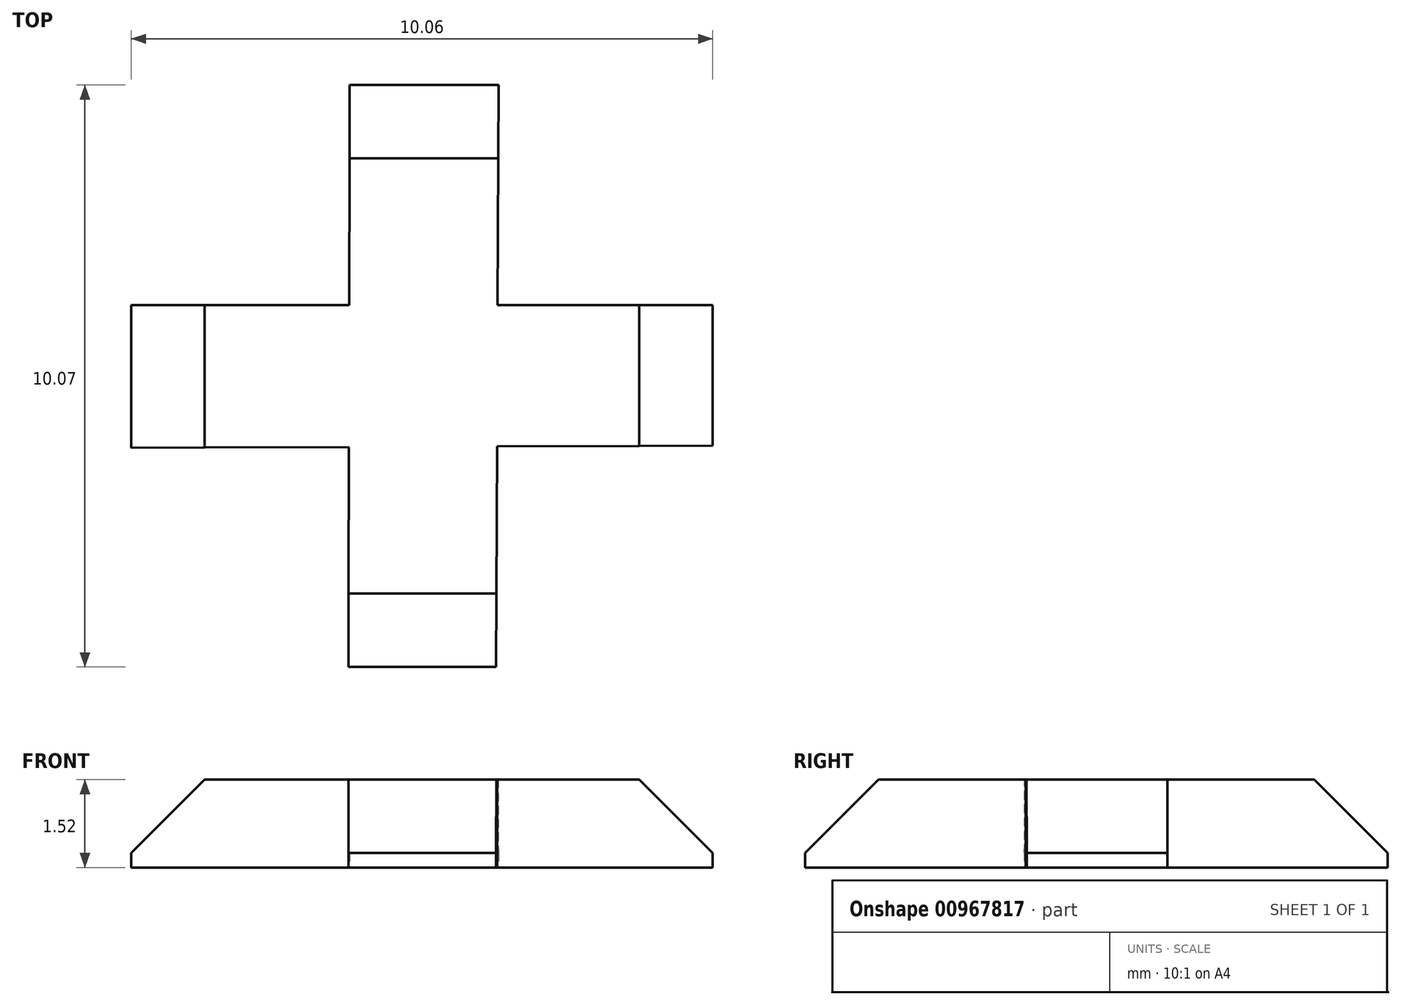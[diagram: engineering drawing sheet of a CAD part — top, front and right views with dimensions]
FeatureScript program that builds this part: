
annotation { "Feature Type Name" : "Feature", "Feature Type Description" : "" }
export const myFeature = defineFeature(function(context is Context, id is Id, definition is map)
    precondition{}
    {
        {
            var Q0;
            Q0=qCreatedBy(makeId("Top.planeOp"),FACE);
            var sketch = newSketch(context, id + "F0", { "sketchPlane" : qUnion([Q0])});
            skLineSegment(sketch, "E0", {"start": v(-5.06, 0) * mm, "end": v(-5.06, 1.2) * mm});
            skLineSegment(sketch, "E1", {"start": v(-5.06, 0) * mm, "end": v(-5.06, -1.27) * mm});
            skLineSegment(sketch, "E2", {"start": v(0, 5.01) * mm, "end": v(-1.28, 5.01) * mm});
            skLineSegment(sketch, "E3", {"start": v(0, 5.01) * mm, "end": v(1.3, 5.01) * mm});
            skLineSegment(sketch, "E4", {"start": v(5, 0) * mm, "end": v(5, 1.2) * mm});
            skLineSegment(sketch, "E5", {"start": v(0, -5.06) * mm, "end": v(1.25, -5.06) * mm});
            skLineSegment(sketch, "E6", {"start": v(5, 0) * mm, "end": v(5, -1.23) * mm});
            skLineSegment(sketch, "E7", {"start": v(0, -5.06) * mm, "end": v(-1.3, -5.06) * mm});
            skLineSegment(sketch, "E8", {"start": v(-5.06, 1.2) * mm, "end": v(-1.3, 1.2) * mm});
            skLineSegment(sketch, "E9", {"start": v(5, -1.23) * mm, "end": v(1.27, -1.24) * mm});
            skLineSegment(sketch, "E10", {"start": v(-1.28, 5.01) * mm, "end": v(-1.3, 1.2) * mm});
            skLineSegment(sketch, "E11", {"start": v(1.25, -5.06) * mm, "end": v(1.27, -1.24) * mm});
            skLineSegment(sketch, "E12.trimOffspring", {"start": v(1.28, 1.2) * mm, "end": v(5, 1.2) * mm});
            skLineSegment(sketch, "E13.trimOffspring", {"start": v(1.28, 1.2) * mm, "end": v(1.3, 5.01) * mm});
            skLineSegment(sketch, "E14.trimOffspring", {"start": v(-1.3, -1.25) * mm, "end": v(-5.06, -1.27) * mm});
            skLineSegment(sketch, "E15.trimOffspring", {"start": v(-1.3, -1.25) * mm, "end": v(-1.3, -5.06) * mm});
            skPoint(sketch, "E16.start.orphan", {"position": v(0, 0) * mm});
            skSolve(sketch);
        }
        {
            var Q0;
            Q0=makeQuery(id+"F0.imprint","IMPRINT",FACE,{"disambiguationData":[TD([[makeQuery(id+"F0.imprint","IMPRINT",EDGE,{"derivedFrom":sQuery(id+"F0.wireOp",EDGE,"E0")}),-1.0]])]});
            extrude(context, id + "F1", {"entities" : qUnion([Q0]), "depth" : 1.52 * mm, "offsetDistance" : 25.4 * mm});
        }
        {
            var Q0;
            Q0=makeQuery(id+"F1.opExtrude","CAP_EDGE",EDGE,{"disambiguationData":[OSD([sQuery(id+"F0.wireOp",EDGE,"E5"),sQuery(id+"F0.wireOp",EDGE,"E7")])],"isStart":false});
            var Q1;
            Q1=makeQuery(id+"F1.opExtrude","CAP_EDGE",EDGE,{"disambiguationData":[OSD([sQuery(id+"F0.wireOp",EDGE,"E0"),sQuery(id+"F0.wireOp",EDGE,"E1")])],"isStart":false});
            var Q2;
            Q2=makeQuery(id+"F1.opExtrude","CAP_EDGE",EDGE,{"disambiguationData":[OSD([sQuery(id+"F0.wireOp",EDGE,"E2"),sQuery(id+"F0.wireOp",EDGE,"E3")])],"isStart":false});
            var Q3;
            Q3=makeQuery(id+"F1.opExtrude","CAP_EDGE",EDGE,{"disambiguationData":[OSD([sQuery(id+"F0.wireOp",EDGE,"E4"),sQuery(id+"F0.wireOp",EDGE,"E6")])],"isStart":false});
            chamfer(context, id + "F2", {"entities" : qUnion([Q0, Q1, Q2, Q3]), "width" : 1.27 * mm, "tangentPropagation" : true});
        }
    });
